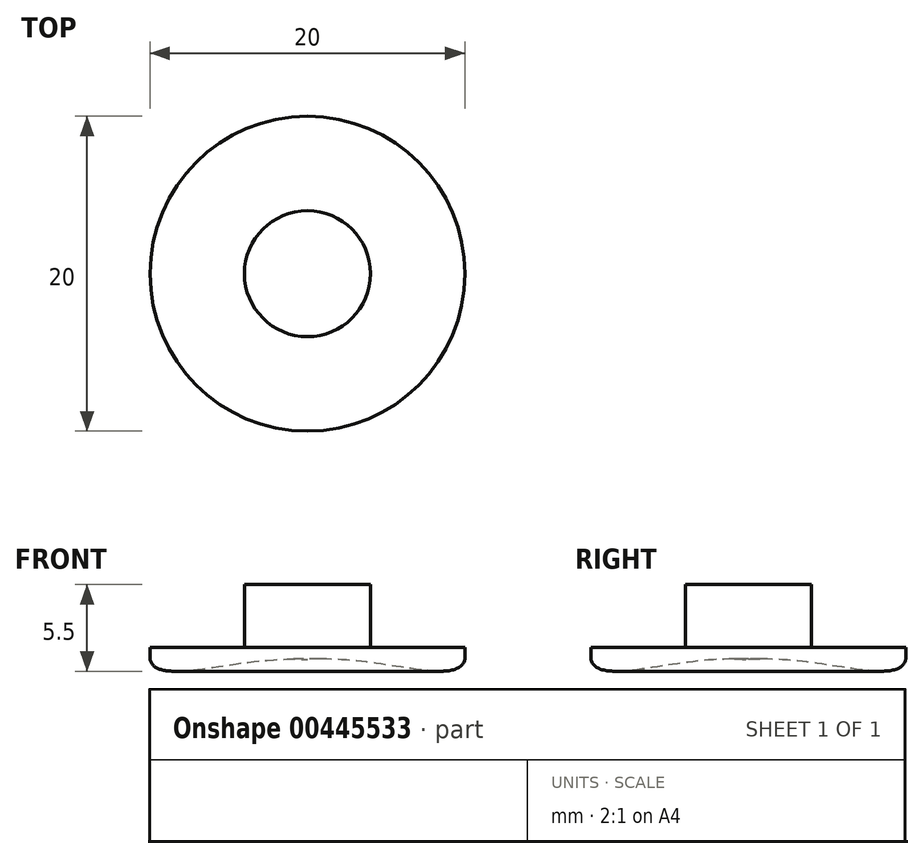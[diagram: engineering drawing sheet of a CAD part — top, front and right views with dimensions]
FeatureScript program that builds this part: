
annotation { "Feature Type Name" : "Feature", "Feature Type Description" : "" }
export const myFeature = defineFeature(function(context is Context, id is Id, definition is map)
    precondition{}
    {
        {
            var Q0;
            Q0=qCreatedBy(makeId("Front.planeOp"),FACE);
            var sketch = newSketch(context, id + "F0", { "sketchPlane" : qUnion([Q0])});
            skFitSpline(sketch, "E0", {"points": [v(-10, 0.75) * mm, v(-8.26, 0) * mm, v(0, 0.75) * mm], "startDerivative": vector(1.23, -5.49) * mm, "endDerivative": vector(14.69, -0.78) * mm});
            skLineSegment(sketch, "E1", {"start": v(-10, 1.5) * mm, "end": v(-4, 1.5) * mm});
            skLineSegment(sketch, "E2", {"start": v(-4, 1.5) * mm, "end": v(-4, 5.5) * mm});
            skLineSegment(sketch, "E3", {"start": v(-4, 5.5) * mm, "end": v(0, 5.5) * mm});
            skLineSegment(sketch, "E4", {"start": v(0, 5.5) * mm, "end": v(0, 0.75) * mm});
            skLineSegment(sketch, "E5", {"start": v(-10, 1.5) * mm, "end": v(-10, 0.75) * mm});
            skSolve(sketch);
        }
        {
            var Q0;
            Q0=makeQuery(id+"F0.imprint","IMPRINT",FACE,{"disambiguationData":[TD([[makeQuery(id+"F0.imprint","IMPRINT",EDGE,{"derivedFrom":sQuery(id+"F0.wireOp",EDGE,"E0")}),1.0]])]});
            var Q1;
            Q1=sQuery(id+"F0.wireOp",EDGE,"E4");
            revolve(context, id + "F1", {"entities" : qUnion([Q0]), "axis" : qUnion([Q1]), "revolveType" : RevolveType.FULL});
        }
        {
            var Q0;
            Q0=makeQuery(id+"F1.opRevolve","SWEPT_EDGE",EDGE,{"disambiguationData":[OSD([sQuery(id+"F0.wireOp",EDGE,"E0"),sQuery(id+"F0.wireOp",EDGE,"E5")])]});
            fillet(context, id + "F2", {"entities" : qUnion([Q0]), "radius" : .5 * mm, "tangentPropagation" : true, "allowEdgeOverflow" : false});
        }
    });
